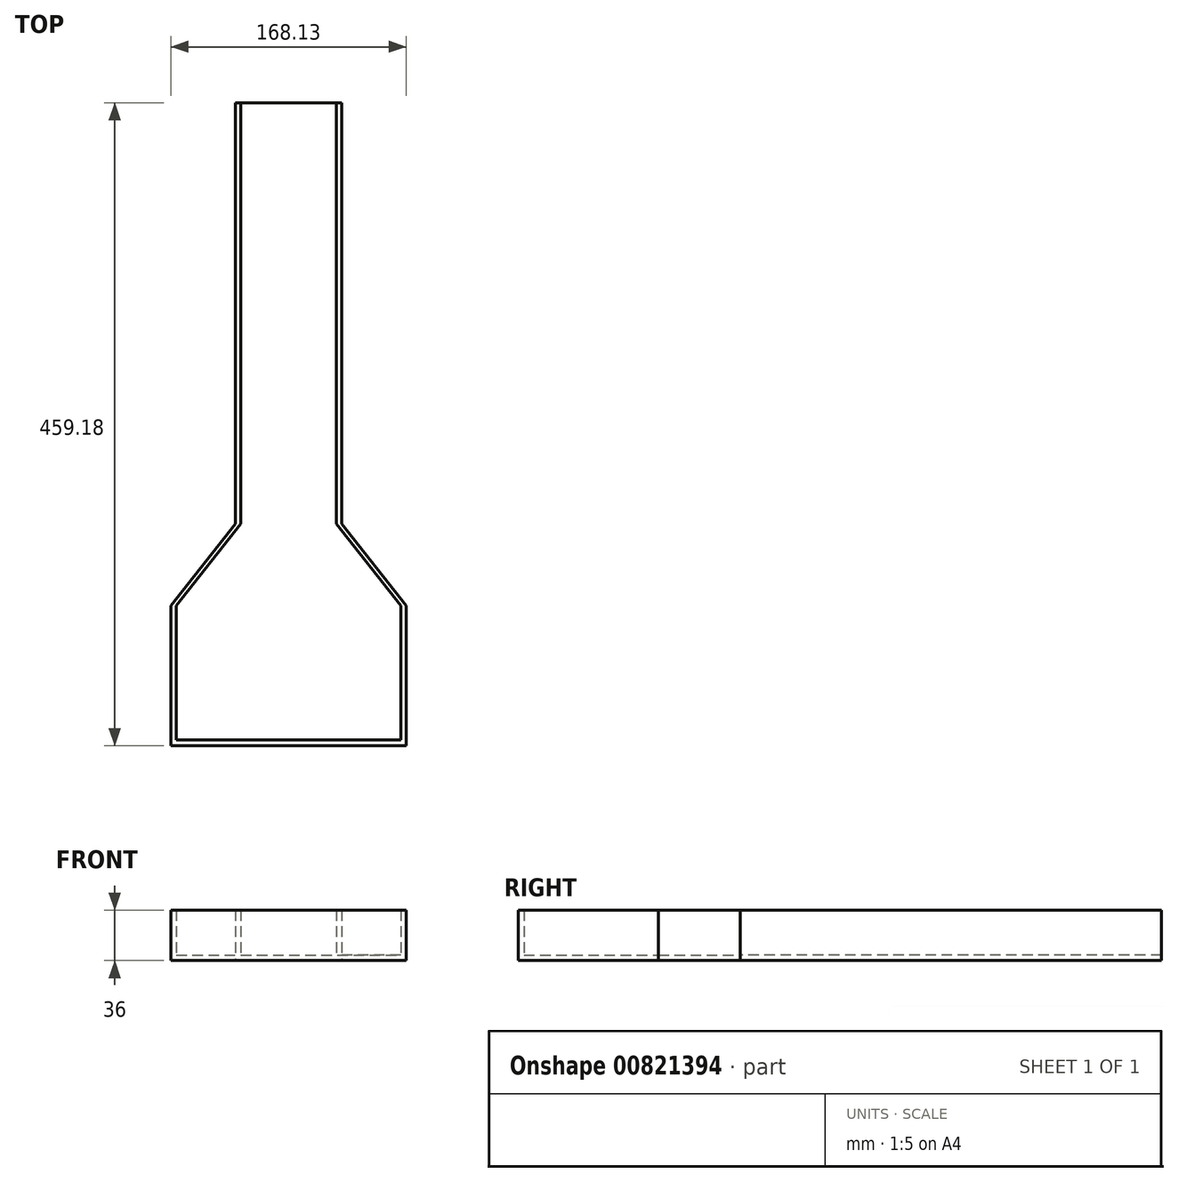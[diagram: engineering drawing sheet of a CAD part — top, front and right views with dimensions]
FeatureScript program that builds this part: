
annotation { "Feature Type Name" : "Feature", "Feature Type Description" : "" }
export const myFeature = defineFeature(function(context is Context, id is Id, definition is map)
    precondition{}
    {
        {
            var Q0;
            Q0=qCreatedBy(makeId("Top.planeOp"),FACE);
            var sketch = newSketch(context, id + "F0", { "sketchPlane" : qUnion([Q0])});
            skLineSegment(sketch, "E0", {"start": v(-52.88, -27.13) * mm, "end": v(-52.88, 72.87) * mm});
            skLineSegment(sketch, "E1", {"start": v(-52.88, 72.87) * mm, "end": v(-6.88, 131.38) * mm});
            skLineSegment(sketch, "E2", {"start": v(-6.88, 131.38) * mm, "end": v(-6.88, 432.05) * mm});
            skLineSegment(sketch, "E3", {"start": v(69.25, 131.38) * mm, "end": v(69.25, 432.05) * mm});
            skLineSegment(sketch, "E4", {"start": v(-6.88, 432.05) * mm, "end": v(69.25, 432.05) * mm});
            skLineSegment(sketch, "E5", {"start": v(-6.88, 432.05) * mm, "end": v(-2.88, 432.05) * mm});
            skLineSegment(sketch, "E6", {"start": v(69.25, 432.05) * mm, "end": v(65.25, 432.05) * mm});
            skLineSegment(sketch, "E7", {"start": v(115.25, 72.88) * mm, "end": v(69.25, 131.38) * mm});
            skLineSegment(sketch, "E8", {"start": v(115.25, 72.88) * mm, "end": v(115.25, -27.13) * mm});
            skLineSegment(sketch, "E9", {"start": v(115.25, -27.13) * mm, "end": v(-52.88, -27.13) * mm});
            skLineSegment(sketch, "E10", {"start": v(-2.88, 432.05) * mm, "end": v(-2.88, 131.38) * mm});
            skLineSegment(sketch, "E11", {"start": v(65.25, 432.05) * mm, "end": v(65.25, 131.38) * mm});
            skLineSegment(sketch, "E12", {"start": v(-48.88, 72.87) * mm, "end": v(-2.88, 131.38) * mm});
            skLineSegment(sketch, "E13", {"start": v(111.25, 72.88) * mm, "end": v(65.25, 131.38) * mm});
            skLineSegment(sketch, "E14", {"start": v(-48.88, -23.13) * mm, "end": v(111.25, -23.13) * mm});
            skLineSegment(sketch, "E15", {"start": v(111.25, -23.13) * mm, "end": v(111.25, 72.88) * mm});
            skLineSegment(sketch, "E16", {"start": v(-48.88, -23.13) * mm, "end": v(-48.88, 72.87) * mm});
            skSolve(sketch);
        }
        {
            var Q0;
            Q0=makeQuery(id+"F0.imprint","IMPRINT",FACE,{"disambiguationData":[TD([[makeQuery(id+"F0.imprint","IMPRINT",EDGE,{"derivedFrom":sQuery(id+"F0.wireOp",EDGE,"E0")}),-1.0]])]});
            extrude(context, id + "F1", {"entities" : qUnion([Q0]), "depth" : 36 * mm, "offsetDistance" : 25 * mm});
        }
        {
            var Q0;
            {var subQ1=sQuery(id+"F0.wireOp",EDGE,"E10");Q0=makeQuery(id+"F0.imprint","IMPRINT",FACE,{"disambiguationData":[TD([[makeQuery(id+"F0.imprint","IMPRINT",EDGE,{"derivedFrom":subQ1}),1.0]])]});}
            extrude(context, id + "F2", {"entities" : qUnion([Q0]), "operationType" : NewBodyOperationType.ADD, "depth" : 4 * mm, "offsetDistance" : 25 * mm});
        }
    });
